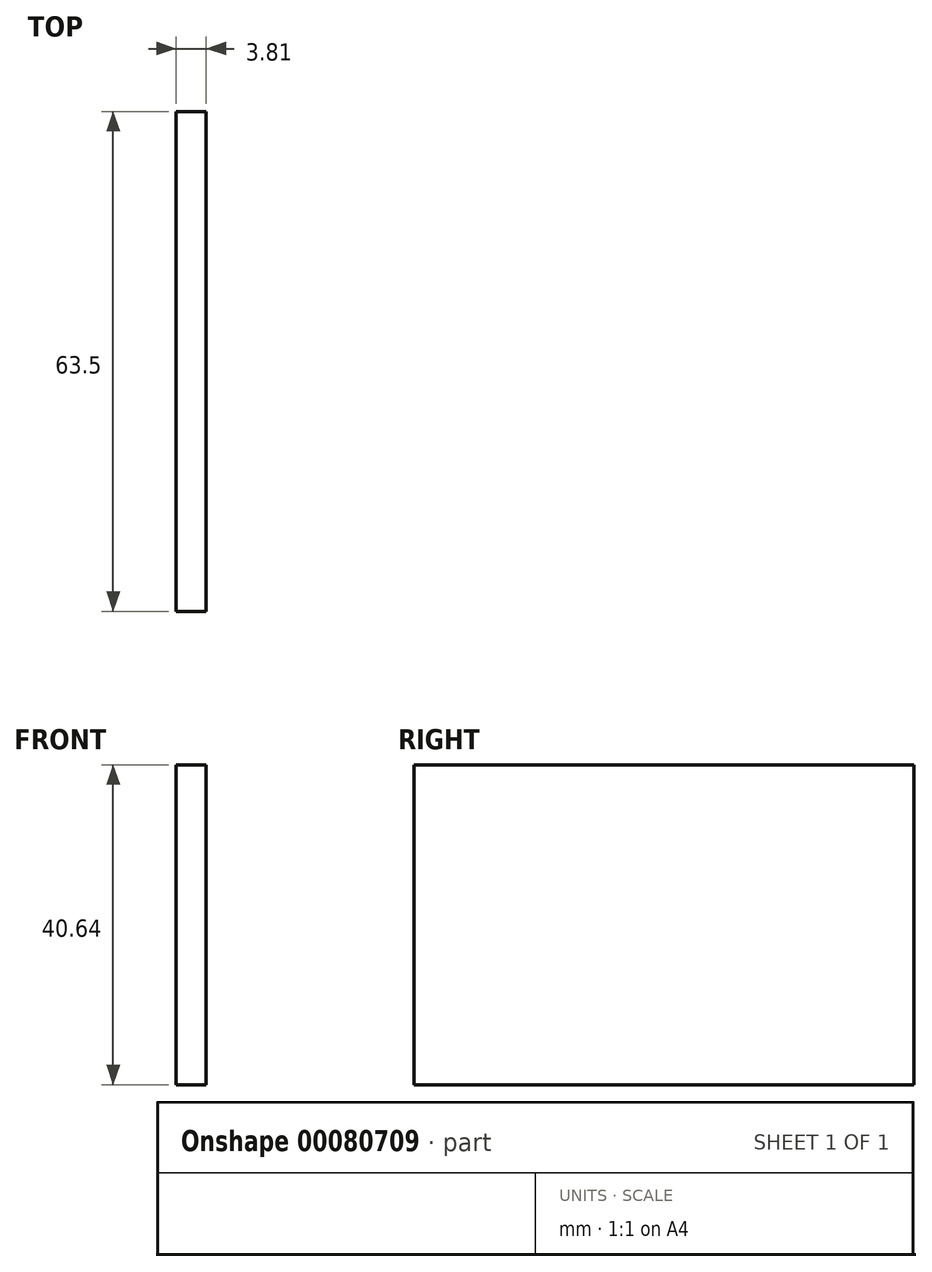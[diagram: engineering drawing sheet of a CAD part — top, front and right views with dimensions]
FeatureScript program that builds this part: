
annotation { "Feature Type Name" : "Feature", "Feature Type Description" : "" }
export const myFeature = defineFeature(function(context is Context, id is Id, definition is map)
    precondition{}
    {
        {
            var Q0;
            Q0=qCreatedBy(makeId("Right.planeOp"),FACE);
            var sketch = newSketch(context, id + "F0", { "sketchPlane" : qUnion([Q0])});
            skLineSegment(sketch, "E0.bottom", {"start": v(31.75, -20.32) * mm, "end": v(-31.75, -20.32) * mm});
            skLineSegment(sketch, "E0.top", {"start": v(31.75, 20.32) * mm, "end": v(-31.75, 20.32) * mm});
            skLineSegment(sketch, "E0.left", {"start": v(31.75, -20.32) * mm, "end": v(31.75, 20.32) * mm});
            skLineSegment(sketch, "E0.right", {"start": v(-31.75, -20.32) * mm, "end": v(-31.75, 20.32) * mm});
            skPoint(sketch, "E0.middle", {"position": v(0, 0) * mm});
            skSolve(sketch);
        }
        {
            var Q0;
            Q0=makeQuery(id+"F0.imprint","IMPRINT",FACE,{"disambiguationData":[TD([[makeQuery(id+"F0.imprint","IMPRINT",EDGE,{"derivedFrom":sQuery(id+"F0.wireOp",EDGE,"E0.bottom")}),-1.0]])]});
            extrude(context, id + "F1", {"entities" : qUnion([Q0]), "depth" : 3.8 * mm});
        }
    });
